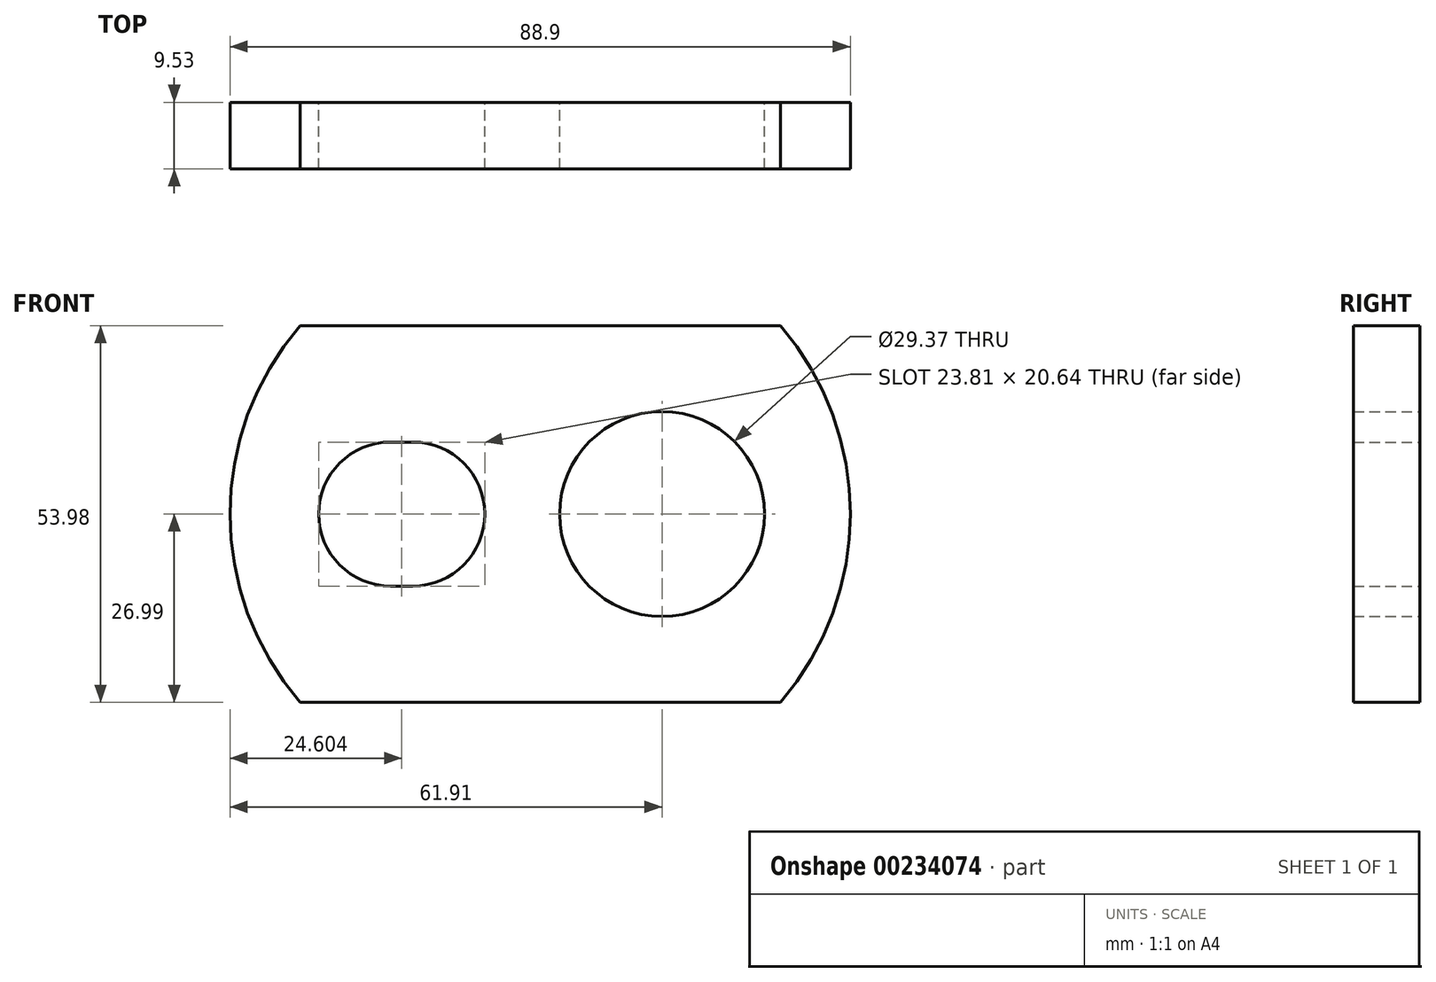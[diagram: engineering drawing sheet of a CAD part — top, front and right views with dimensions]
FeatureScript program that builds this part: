
annotation { "Feature Type Name" : "Feature", "Feature Type Description" : "" }
export const myFeature = defineFeature(function(context is Context, id is Id, definition is map)
    precondition{}
    {
        {
            var Q0;
            Q0=qCreatedBy(makeId("Front.planeOp"),FACE);
            var sketch = newSketch(context, id + "F0", { "sketchPlane" : qUnion([Q0])});
            skLineSegment(sketch, "E0", {"start": v(16.94, -26.99) * mm, "end": v(-51.87, -26.99) * mm});
            skLineSegment(sketch, "E1", {"start": v(-51.87, 26.99) * mm, "end": v(16.94, 26.99) * mm});
            skCircle(sketch, "E2", {"center": v(0, 0) * mm, "radius": 14.68 * mm});
            skLineSegment(sketch, "E3", {"start": v(26.99, 0) * mm, "end": v(-61.91, 0) * mm, "construction": true});
            skArc(sketch, "E4", {"start": v(16.94, 26.99) * mm, "mid": v(26.99, 0) * mm, "end": v(16.94, -26.99) * mm});
            skArc(sketch, "E5", {"start": v(-51.87, 26.99) * mm, "mid": v(-61.91, 0) * mm, "end": v(-51.87, -26.99) * mm});
            skArc(sketch, "E6", {"start": v(-38.9, 10.32) * mm, "mid": v(-49.21, 0) * mm, "end": v(-38.9, -10.32) * mm});
            skArc(sketch, "E7", {"start": v(-35.72, -10.32) * mm, "mid": v(-25.4, 0) * mm, "end": v(-35.72, 10.32) * mm});
            skLineSegment(sketch, "E8", {"start": v(0, 26.99) * mm, "end": v(0, -26.99) * mm, "construction": true});
            skLineSegment(sketch, "E9", {"start": v(-35.72, -10.32) * mm, "end": v(-38.9, -10.32) * mm});
            skLineSegment(sketch, "E10", {"start": v(-38.9, 10.32) * mm, "end": v(-35.72, 10.32) * mm});
            skLineSegment(sketch, "E11", {"start": v(-38.9, -10.32) * mm, "end": v(-38.9, 10.32) * mm, "construction": true});
            skLineSegment(sketch, "E12", {"start": v(-35.72, -10.32) * mm, "end": v(-35.72, 10.32) * mm, "construction": true});
            skSolve(sketch);
        }
        {
            var Q0;
            Q0 = qSketchRegion(id + "F0", true);
            extrude(context, id + "F1", {"entities" : qUnion([Q0]), "depth" : 9.52 * mm});
        }
    });
